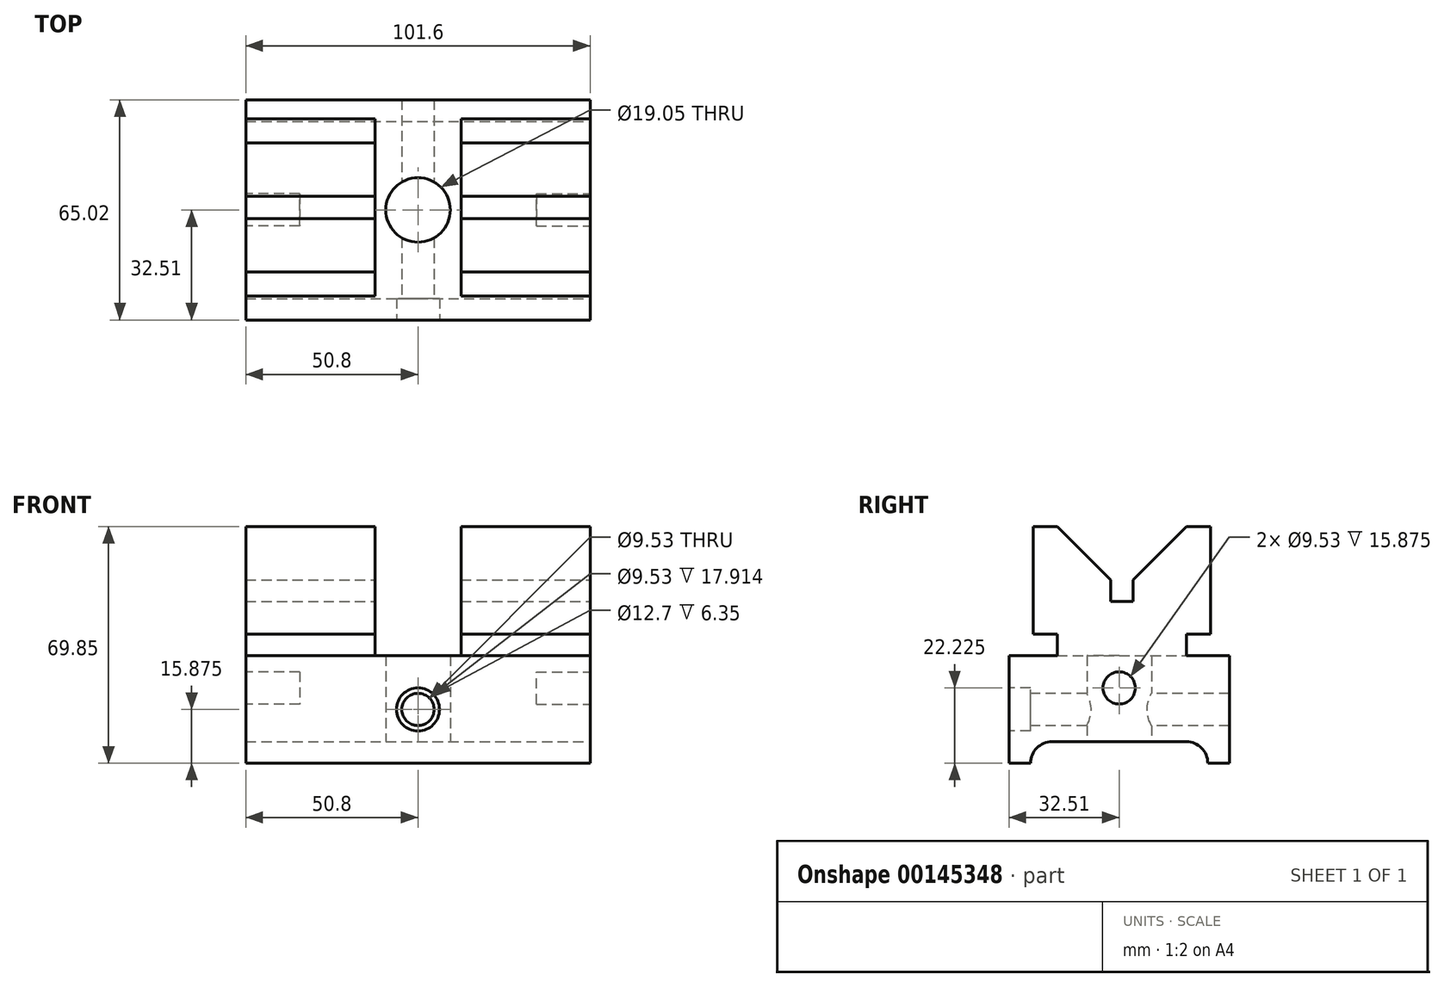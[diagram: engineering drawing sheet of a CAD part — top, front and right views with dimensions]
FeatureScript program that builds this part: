
annotation { "Feature Type Name" : "Feature", "Feature Type Description" : "" }
export const myFeature = defineFeature(function(context is Context, id is Id, definition is map)
    precondition{}
    {
        {
            var Q0;
            Q0=qCreatedBy(makeId("Top.planeOp"),FACE);
            var sketch = newSketch(context, id + "F0", { "sketchPlane" : qUnion([Q0])});
            skLineSegment(sketch, "E0.bottom", {"start": v(50.8, -32.51) * mm, "end": v(-50.8, -32.51) * mm});
            skLineSegment(sketch, "E0.top", {"start": v(50.8, 32.51) * mm, "end": v(-50.8, 32.51) * mm});
            skLineSegment(sketch, "E0.left", {"start": v(50.8, -32.51) * mm, "end": v(50.8, 32.51) * mm});
            skLineSegment(sketch, "E0.right", {"start": v(-50.8, -32.51) * mm, "end": v(-50.8, 32.51) * mm});
            skPoint(sketch, "E0.middle", {"position": v(0, 0) * mm});
            skCircle(sketch, "E1", {"center": v(0, 0) * mm, "radius": 9.53 * mm});
            skSolve(sketch);
        }
        {
            var Q0;
            Q0 = qSketchRegion(id + "F0", true);
            extrude(context, id + "F1", {"entities" : qUnion([Q0]), "depth" : 31.75 * mm});
        }
        {
            var Q0;
            Q0=makeQuery(id+"F1.opExtrude","SWEPT_FACE",FACE,{"disambiguationData":[OSD([sQuery(id+"F0.wireOp",EDGE,"E0.left")])]});
            var sketch = newSketch(context, id + "F2", { "sketchPlane" : qUnion([Q0])});
            skLineSegment(sketch, "E2", {"start": v(-19.81, 6.35) * mm, "end": v(19.81, 6.35) * mm});
            skLineSegment(sketch, "E3", {"start": v(-32.51, 0) * mm, "end": v(-26.16, 0) * mm});
            skLineSegment(sketch, "E4", {"start": v(32.51, 0) * mm, "end": v(26.16, 0) * mm});
            skArc(sketch, "E5", {"start": v(-19.81, 6.35) * mm, "mid": v(-24.3, 4.5) * mm, "end": v(-26.16, 0) * mm});
            skArc(sketch, "E6", {"start": v(19.81, 6.35) * mm, "mid": v(24.3, 4.5) * mm, "end": v(26.16, 0) * mm});
            skLineSegment(sketch, "E7", {"start": v(26.16, 0) * mm, "end": v(-26.16, 0) * mm});
            skSolve(sketch);
        }
        {
            var Q0;
            Q0 = qSketchRegion(id + "F2", true);
            extrude(context, id + "F3", {"entities" : qUnion([Q0]), "operationType" : NewBodyOperationType.REMOVE, "endBound" : BoundingType.THROUGH_ALL, "oppositeDirection" : true, "depth" : 25.4 * mm});
        }
        {
            var Q0;
            Q0=makeQuery(id+"F1.opExtrude","SWEPT_FACE",FACE,{"disambiguationData":[OSD([sQuery(id+"F0.wireOp",EDGE,"E0.left")])]});
            var sketch = newSketch(context, id + "F4", { "sketchPlane" : qUnion([Q0])});
            skLineSegment(sketch, "E8", {"start": v(-18.29, 31.75) * mm, "end": v(-18.29, 38.1) * mm});
            skLineSegment(sketch, "E9", {"start": v(-18.29, 38.1) * mm, "end": v(-25.4, 38.1) * mm});
            skLineSegment(sketch, "E10", {"start": v(-25.4, 38.1) * mm, "end": v(-25.4, 69.85) * mm});
            skLineSegment(sketch, "E11", {"start": v(-25.4, 69.85) * mm, "end": v(-18.29, 69.85) * mm});
            skLineSegment(sketch, "E12", {"start": v(-18.29, 69.85) * mm, "end": v(-2.54, 54.1) * mm});
            skLineSegment(sketch, "E13", {"start": v(-2.54, 54.1) * mm, "end": v(-2.54, 47.75) * mm});
            skLineSegment(sketch, "E14", {"start": v(-2.54, 47.75) * mm, "end": v(4.06, 47.75) * mm});
            skLineSegment(sketch, "E15", {"start": v(4.06, 47.75) * mm, "end": v(4.06, 54.1) * mm});
            skLineSegment(sketch, "E16", {"start": v(4.06, 54.1) * mm, "end": v(19.81, 69.85) * mm});
            skLineSegment(sketch, "E17", {"start": v(19.81, 69.85) * mm, "end": v(26.92, 69.85) * mm});
            skLineSegment(sketch, "E18", {"start": v(26.92, 69.85) * mm, "end": v(26.92, 38.1) * mm});
            skLineSegment(sketch, "E19", {"start": v(26.92, 38.1) * mm, "end": v(19.81, 38.1) * mm});
            skLineSegment(sketch, "E20", {"start": v(19.81, 38.1) * mm, "end": v(19.81, 31.75) * mm});
            skLineSegment(sketch, "E21", {"start": v(-18.29, 31.75) * mm, "end": v(19.81, 31.75) * mm});
            skSolve(sketch);
        }
        {
            var Q0;
            Q0=makeQuery(id+"F4.imprint","IMPRINT",FACE,{"disambiguationData":[TD([[makeQuery(id+"F4.imprint","IMPRINT",EDGE,{"derivedFrom":sQuery(id+"F4.wireOp",EDGE,"E8")}),-1.0]])]});
            var Q1;
            Q1=makeQuery(id+"F1.opExtrude","SWEPT_FACE",FACE,{"disambiguationData":[OSD([sQuery(id+"F0.wireOp",EDGE,"E0.right")])]});
            var Q2;
            Q2=makeQuery(id+"F1.opExtrude","SWEPT_FACE",FACE,{"disambiguationData":[OSD([sQuery(id+"F0.wireOp",EDGE,"E0.left")])]});
            extrude(context, id + "F5", {"entities" : qUnion([Q0]), "operationType" : NewBodyOperationType.ADD, "endBound" : BoundingType.UP_TO_SURFACE, "oppositeDirection" : true, "endBoundEntityFace" : qUnion([Q1]), "depth" : 38.1 * mm, "hasSecondDirection" : true, "secondDirectionOppositeDirection" : true, "secondDirectionBoundEntityFace" : qUnion([Q2]), "secondDirectionDepth" : 63.5 * mm});
        }
        {
            var Q0;
            Q0 = qSketchRegion(id + "F4", true);
            extrude(context, id + "F6", {"entities" : qUnion([Q0]), "operationType" : NewBodyOperationType.ADD, "oppositeDirection" : true, "depth" : 38.1 * mm});
        }
        {
            var Q0;
            Q0=makeQuery(id+"F6.boolean.opBoolean","MERGE",FACE,{"derivedFrom":[makeQuery(id+"F1.opExtrude","SWEPT_FACE",FACE,{"disambiguationData":[OSD([sQuery(id+"F0.wireOp",EDGE,"E0.left")])]}),makeQuery(id+"F6.opExtrude","CAP_FACE",FACE,{"disambiguationData":[OSD([sQuery(id+"F4.wireOp",EDGE,"E8"),sQuery(id+"F4.wireOp",EDGE,"E9"),sQuery(id+"F4.wireOp",EDGE,"E10"),sQuery(id+"F4.wireOp",EDGE,"E11"),sQuery(id+"F4.wireOp",EDGE,"E12"),sQuery(id+"F4.wireOp",EDGE,"E13"),sQuery(id+"F4.wireOp",EDGE,"E14"),sQuery(id+"F4.wireOp",EDGE,"E15"),sQuery(id+"F4.wireOp",EDGE,"E16"),sQuery(id+"F4.wireOp",EDGE,"E17"),sQuery(id+"F4.wireOp",EDGE,"E18"),sQuery(id+"F4.wireOp",EDGE,"E19"),sQuery(id+"F4.wireOp",EDGE,"E20"),sQuery(id+"F4.wireOp",EDGE,"E21")])],"isStart":true})]});
            var sketch = newSketch(context, id + "F7", { "sketchPlane" : qUnion([Q0])});
            skCircle(sketch, "E22", {"center": v(0, 22.23) * mm, "radius": 4.76 * mm});
            skSolve(sketch);
        }
        {
            var Q0;
            Q0=makeQuery(id+"F7.imprint","IMPRINT",FACE,{"disambiguationData":[TD([[makeQuery(id+"F7.imprint","IMPRINT",EDGE,{"derivedFrom":sQuery(id+"F7.wireOp",EDGE,"E22")}),1.0]])]});
            extrude(context, id + "F8", {"entities" : qUnion([Q0]), "operationType" : NewBodyOperationType.REMOVE, "oppositeDirection" : true, "depth" : 15.88 * mm});
        }
        {
            var Q0;
            {var subQ0=sQuery(id+"F0.wireOp",EDGE,"E0.right");Q0=makeQuery(id+"F5.boolean.opBoolean","MERGE",FACE,{"derivedFrom":[makeQuery(id+"F1.opExtrude","SWEPT_FACE",FACE,{"disambiguationData":[OSD([subQ0])]}),makeQuery(id+"F5.opExtrude","CAP_FACE",FACE,{"disambiguationData":[OSD([subQ0])],"isStart":false})]});}
            var sketch = newSketch(context, id + "F9", { "sketchPlane" : qUnion([Q0])});
            skCircle(sketch, "E23", {"center": v(0, 22.23) * mm, "radius": 4.76 * mm});
            skSolve(sketch);
        }
        {
            var Q0;
            Q0 = qSketchRegion(id + "F9", true);
            extrude(context, id + "F10", {"entities" : qUnion([Q0]), "operationType" : NewBodyOperationType.REMOVE, "oppositeDirection" : true, "depth" : 15.88 * mm});
        }
        {
            var Q0;
            Q0=makeQuery(id+"F1.opExtrude","SWEPT_FACE",FACE,{"disambiguationData":[OSD([sQuery(id+"F0.wireOp",EDGE,"E0.bottom")])]});
            var sketch = newSketch(context, id + "F11", { "sketchPlane" : qUnion([Q0])});
            skCircle(sketch, "E24", {"center": v(0, 15.88) * mm, "radius": 4.76 * mm});
            skSolve(sketch);
        }
        {
            var Q0;
            Q0=sQuery(id+"F11.wireOp",VERTEX,"E24.center");
            var Q1;
            Q1=makeQuery(id+"F1.opExtrude","SWEPT_BODY",BODY,{"disambiguationData":[OSD([sQuery(id+"F0.wireOp",EDGE,"E0.bottom"),sQuery(id+"F0.wireOp",EDGE,"E0.top"),sQuery(id+"F0.wireOp",EDGE,"E0.left"),sQuery(id+"F0.wireOp",EDGE,"E0.right"),sQuery(id+"F0.wireOp",EDGE,"E1")])]});
            hole(context, id + "F12", {"style" : HoleStyle.C_BORE, "endStyle" : HoleEndStyle.THROUGH, "holeDiameter" : 9.52 * mm, "cBoreDiameter" : 12.7 * mm, "cBoreDepth" : 6.35 * mm, "locations" : qUnion([Q0]), "scope" : qUnion([Q1]), "isTappedThrough" : true});
        }
    });
